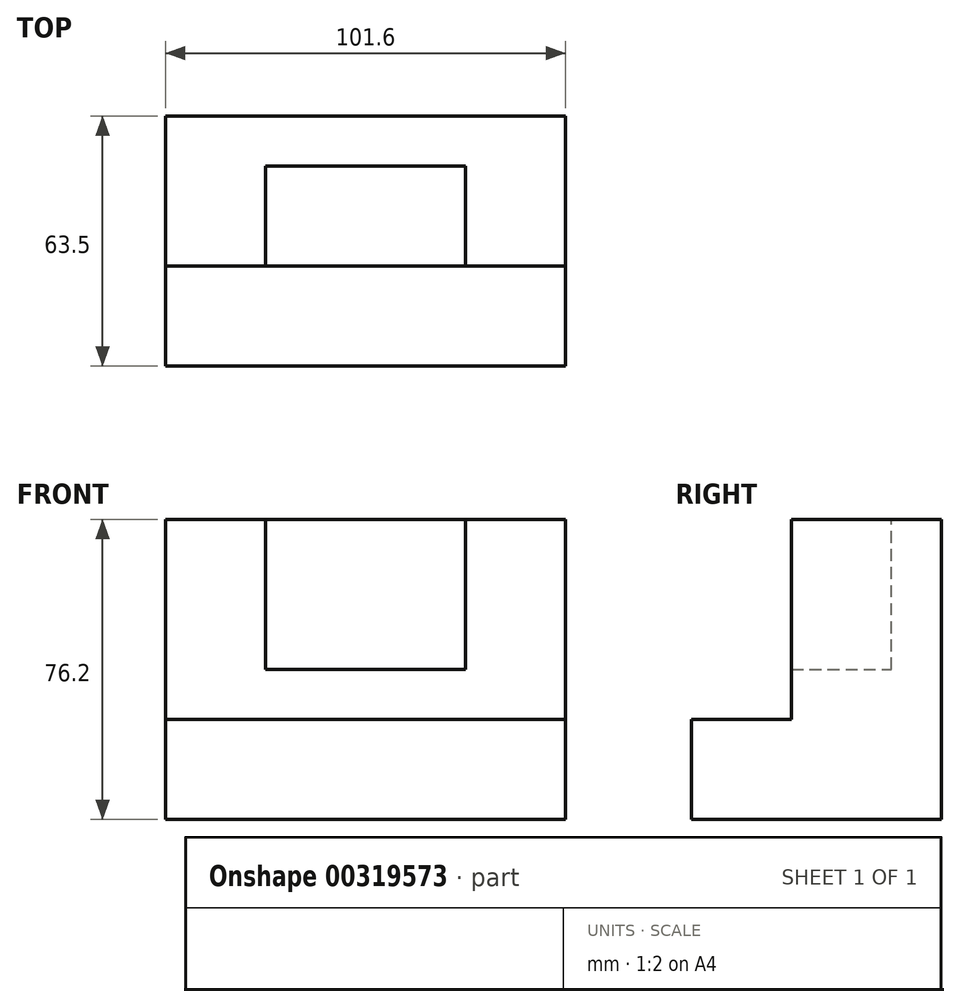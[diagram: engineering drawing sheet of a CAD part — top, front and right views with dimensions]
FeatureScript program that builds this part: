
annotation { "Feature Type Name" : "Feature", "Feature Type Description" : "" }
export const myFeature = defineFeature(function(context is Context, id is Id, definition is map)
    precondition{}
    {
        {
            var Q0;
            Q0=qCreatedBy(makeId("Front.planeOp"),FACE);
            var sketch = newSketch(context, id + "F0", { "sketchPlane" : qUnion([Q0])});
            skLineSegment(sketch, "E0", {"start": v(-48.63, -61.13) * mm, "end": v(52.97, -61.13) * mm});
            skLineSegment(sketch, "E1", {"start": v(-48.63, -61.13) * mm, "end": v(-48.63, 15.07) * mm});
            skLineSegment(sketch, "E2", {"start": v(-48.63, 15.07) * mm, "end": v(52.97, 15.07) * mm});
            skLineSegment(sketch, "E3", {"start": v(52.97, 15.07) * mm, "end": v(52.97, -61.13) * mm});
            skSolve(sketch);
        }
        {
            var Q0;
            Q0=makeQuery(id+"F0.imprint","IMPRINT",FACE,{"disambiguationData":[TD([[makeQuery(id+"F0.imprint","IMPRINT",EDGE,{"derivedFrom":sQuery(id+"F0.wireOp",EDGE,"E0")}),1.0]])]});
            extrude(context, id + "F1", {"entities" : qUnion([Q0]), "depth" : 63.5 * mm});
        }
        {
            var Q0;
            Q0=makeQuery(id+"F1.opExtrude","SWEPT_FACE",FACE,{"disambiguationData":[OSD([sQuery(id+"F0.wireOp",EDGE,"E2")])]});
            var sketch = newSketch(context, id + "F2", { "sketchPlane" : qUnion([Q0])});
            skLineSegment(sketch, "E4", {"start": v(-48.63, -63.5) * mm, "end": v(-48.63, -38.1) * mm});
            skLineSegment(sketch, "E5", {"start": v(-48.63, -38.1) * mm, "end": v(52.97, -38.1) * mm});
            skLineSegment(sketch, "E6", {"start": v(52.97, -38.1) * mm, "end": v(52.97, -63.5) * mm});
            skLineSegment(sketch, "E7", {"start": v(52.97, -63.5) * mm, "end": v(-48.63, -63.5) * mm});
            skSolve(sketch);
        }
        {
            var Q0;
            Q0=makeQuery(id+"F2.imprint","IMPRINT",FACE,{"disambiguationData":[TD([[makeQuery(id+"F2.imprint","IMPRINT",EDGE,{"derivedFrom":sQuery(id+"F2.wireOp",EDGE,"E4")}),-1.0]])]});
            extrude(context, id + "F3", {"entities" : qUnion([Q0]), "operationType" : NewBodyOperationType.REMOVE, "oppositeDirection" : true, "depth" : 50.8 * mm});
        }
        {
            var Q0;
            Q0=makeQuery(id+"F1.opExtrude","SWEPT_FACE",FACE,{"disambiguationData":[OSD([sQuery(id+"F0.wireOp",EDGE,"E2")])]});
            var sketch = newSketch(context, id + "F4", { "sketchPlane" : qUnion([Q0])});
            skLineSegment(sketch, "E8", {"start": v(-23.23, -38.1) * mm, "end": v(27.57, -38.1) * mm});
            skLineSegment(sketch, "E9", {"start": v(-23.23, -38.1) * mm, "end": v(-23.23, -12.7) * mm});
            skLineSegment(sketch, "E10", {"start": v(-23.23, -12.7) * mm, "end": v(27.57, -12.7) * mm});
            skLineSegment(sketch, "E11", {"start": v(27.57, -12.7) * mm, "end": v(27.57, -38.1) * mm});
            skSolve(sketch);
        }
        {
            var Q0;
            Q0=makeQuery(id+"F4.imprint","IMPRINT",FACE,{"disambiguationData":[TD([[makeQuery(id+"F4.imprint","IMPRINT",EDGE,{"derivedFrom":sQuery(id+"F4.wireOp",EDGE,"E8")}),1.0]])]});
            extrude(context, id + "F5", {"entities" : qUnion([Q0]), "operationType" : NewBodyOperationType.REMOVE, "oppositeDirection" : true, "depth" : 38.1 * mm});
        }
    });
